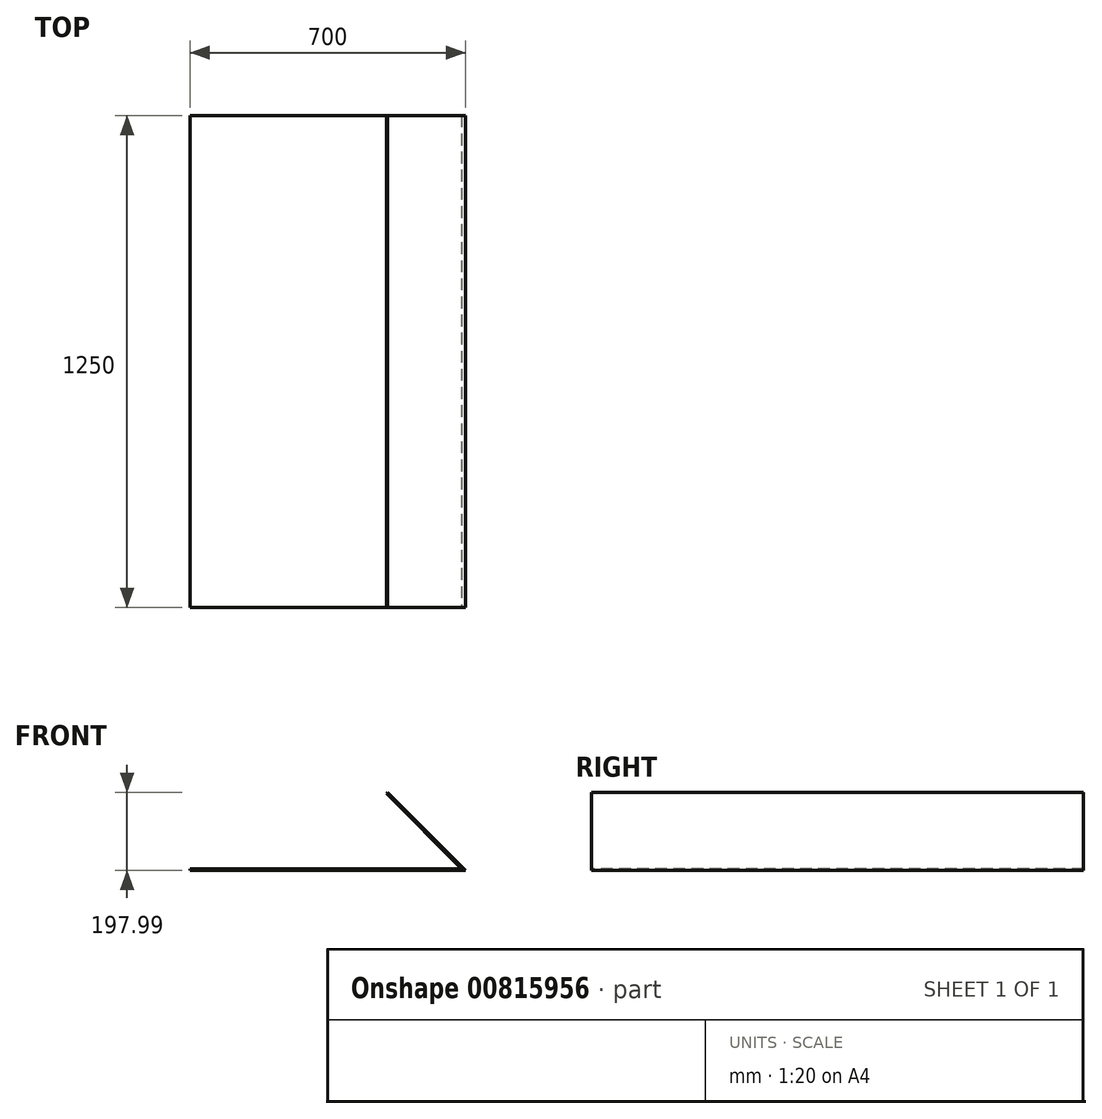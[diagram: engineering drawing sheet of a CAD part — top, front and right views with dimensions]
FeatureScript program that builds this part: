
annotation { "Feature Type Name" : "Feature", "Feature Type Description" : "" }
export const myFeature = defineFeature(function(context is Context, id is Id, definition is map)
    precondition{}
    {
        {
            var Q0;
            Q0=qCreatedBy(makeId("Front.planeOp"),FACE);
            var sketch = newSketch(context, id + "F0", { "sketchPlane" : qUnion([Q0])});
            skLineSegment(sketch, "E0", {"start": v(0, 0) * mm, "end": v(700, 0) * mm});
            skLineSegment(sketch, "E1", {"start": v(700, 0) * mm, "end": v(502.01, 197.99) * mm});
            skLineSegment(sketch, "E2", {"start": v(0, 0) * mm, "end": v(0, 4) * mm});
            skLineSegment(sketch, "E3.0", {"start": v(690.34, 4) * mm, "end": v(499.18, 195.16) * mm});
            skLineSegment(sketch, "E3.1", {"start": v(0, 4) * mm, "end": v(690.34, 4) * mm});
            skLineSegment(sketch, "E4", {"start": v(502.01, 197.99) * mm, "end": v(499.18, 195.16) * mm});
            skSolve(sketch);
        }
        {
            var Q0;
            Q0=qSketchRegion(id+"F0",true);
            extrude(context, id + "F1", {"entities" : qUnion([Q0]), "oppositeDirection" : true, "depth" : 1250 * mm, "offsetDistance" : 25.4 * mm});
        }
    });
